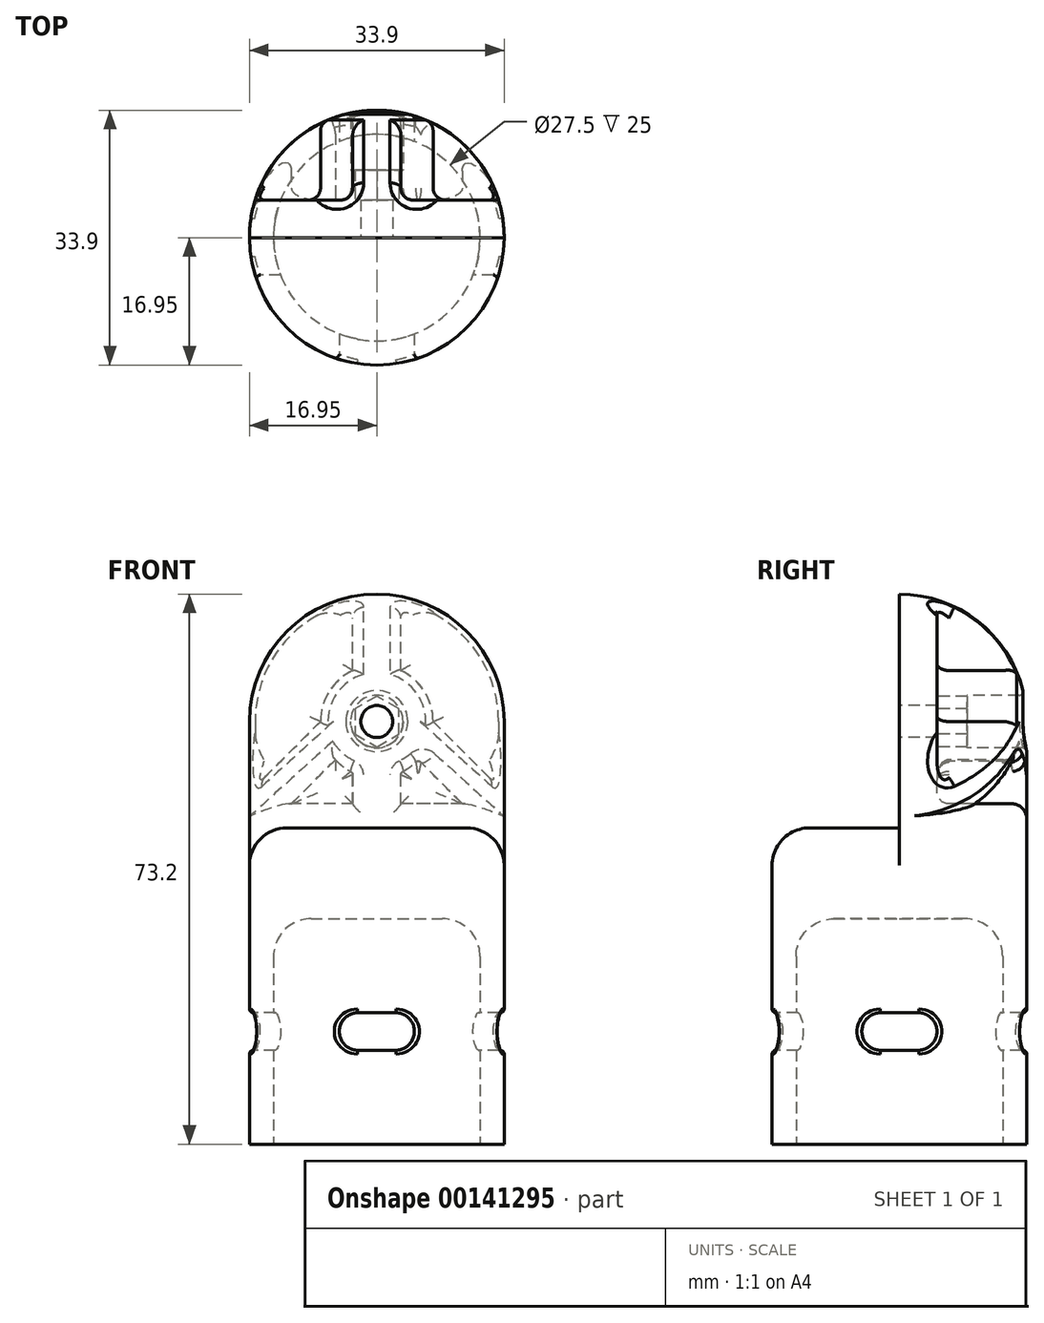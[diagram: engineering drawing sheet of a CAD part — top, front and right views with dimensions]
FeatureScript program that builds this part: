
annotation { "Feature Type Name" : "Feature", "Feature Type Description" : "" }
export const myFeature = defineFeature(function(context is Context, id is Id, definition is map)
    precondition{}
    {
        {
            var Q0;
            Q0=qCreatedBy(makeId("Front.planeOp"),FACE);
            var sketch = newSketch(context, id + "F0", { "sketchPlane" : qUnion([Q0])});
            skLineSegment(sketch, "E0", {"start": v(13.75, 0) * mm, "end": v(13.75, 25) * mm});
            skLineSegment(sketch, "E1", {"start": v(8.75, 30) * mm, "end": v(0, 30) * mm});
            skLineSegment(sketch, "E2", {"start": v(0, 30) * mm, "end": v(0, 33.2) * mm});
            skLineSegment(sketch, "E3", {"start": v(0, 33.2) * mm, "end": v(16.95, 33.2) * mm, "construction": true});
            skLineSegment(sketch, "E4", {"start": v(16.95, 33.2) * mm, "end": v(16.95, 0) * mm});
            skLineSegment(sketch, "E5", {"start": v(16.95, 0) * mm, "end": v(13.75, 0) * mm});
            skPoint(sketch, "E6.visualSharp", {"position": v(13.75, 30) * mm});
            skArc(sketch, "E6.filletArc", {"start": v(13.75, 25) * mm, "mid": v(12.29, 28.54) * mm, "end": v(8.75, 30) * mm});
            skLineSegment(sketch, "E7", {"start": v(16.95, 33.2) * mm, "end": v(16.95, 56.25) * mm});
            skLineSegment(sketch, "E8", {"start": v(0, 73.2) * mm, "end": v(0, 73.2) * mm});
            skLineSegment(sketch, "E9", {"start": v(0, 73.2) * mm, "end": v(0, 33.2) * mm});
            skPoint(sketch, "E10.visualSharp", {"position": v(16.95, 73.2) * mm});
            skArc(sketch, "E10.filletArc", {"start": v(16.95, 56.25) * mm, "mid": v(11.99, 68.24) * mm, "end": v(0, 73.2) * mm});
            skSolve(sketch);
        }
        {
            var Q0;
            Q0=qSketchRegion(id+"F0",true);
            var Q1;
            Q1=sQuery(id+"F0.wireOp",EDGE,"E2");
            revolve(context, id + "F1", {"entities" : qUnion([Q0]), "axis" : qUnion([Q1]), "revolveType" : RevolveType.FULL});
        }
        {
            var Q0;
            Q0=qCreatedBy(makeId("Front.planeOp"),FACE);
            var sketch = newSketch(context, id + "F2", { "sketchPlane" : qUnion([Q0])});
            skArc(sketch, "E11", {"start": v(20.45, 56.25) * mm, "mid": v(0, 76.7) * mm, "end": v(-20.45, 56.25) * mm});
            skLineSegment(sketch, "E12", {"start": v(-20.45, 56.25) * mm, "end": v(-20.45, 42.1) * mm});
            skLineSegment(sketch, "E13", {"start": v(-20.45, 42.1) * mm, "end": v(20.45, 42.1) * mm});
            skLineSegment(sketch, "E14", {"start": v(20.45, 42.1) * mm, "end": v(20.45, 56.25) * mm});
            skSolve(sketch);
        }
        {
            var Q0;
            Q0=qSketchRegion(id+"F2",true);
            extrude(context, id + "F3", {"entities" : qUnion([Q0]), "operationType" : NewBodyOperationType.REMOVE, "depth" : 25 * mm});
        }
        {
            var Q0;
            Q0=qCreatedBy(makeId("Front.planeOp"),FACE);
            cPlane(context, id + "F4", {"entities" : qUnion([Q0]), "cplaneType" : CPlaneType.OFFSET, "offset" : 5 * mm, "oppositeDirection" : true, "width" : 150 * mm, "height" : 150 * mm});
        }
        {
            var Q0;
            Q0=makeQuery(id+"F3.boolean.opBoolean","INTERSECT",EDGE,{"derivedFrom":[makeQuery(id+"F1.opRevolve","SWEPT_FACE",FACE,{"disambiguationData":[OSD([sQuery(id+"F0.wireOp",EDGE,"E4"),sQuery(id+"F0.wireOp",EDGE,"E7")])]}),makeQuery(id+"F3.opExtrude","SWEPT_FACE",FACE,{"disambiguationData":[OSD([sQuery(id+"F2.wireOp",EDGE,"E13")])]})]});
            fillet(context, id + "F5", {"entities" : qUnion([Q0]), "radius" : 5 * mm, "tangentPropagation" : true, "allowEdgeOverflow" : false});
        }
        {
            var Q0;
            Q0=qCreatedBy(makeId("Front.planeOp"),FACE);
            var sketch = newSketch(context, id + "F6", { "sketchPlane" : qUnion([Q0])});
            skLineSegment(sketch, "E15.bottom", {"start": v(2.5, 12.5) * mm, "end": v(-2.5, 12.5) * mm});
            skLineSegment(sketch, "E15.top", {"start": v(2.5, 17.5) * mm, "end": v(-2.5, 17.5) * mm});
            skLineSegment(sketch, "E15.left", {"start": v(5, 15) * mm, "end": v(5, 15) * mm});
            skLineSegment(sketch, "E15.right", {"start": v(-5, 15) * mm, "end": v(-5, 15) * mm});
            skPoint(sketch, "E15.middle", {"position": v(0, 15) * mm});
            skPoint(sketch, "E16.visualSharp", {"position": v(-5, 17.5) * mm});
            skArc(sketch, "E16.filletArc", {"start": v(-2.5, 17.5) * mm, "mid": v(-4.27, 16.77) * mm, "end": v(-5, 15) * mm});
            skPoint(sketch, "E17.visualSharp", {"position": v(-5, 12.5) * mm});
            skArc(sketch, "E17.filletArc", {"start": v(-5, 15) * mm, "mid": v(-4.27, 13.23) * mm, "end": v(-2.5, 12.5) * mm});
            skPoint(sketch, "E18.visualSharp", {"position": v(5, 12.5) * mm});
            skArc(sketch, "E18.filletArc", {"start": v(2.5, 12.5) * mm, "mid": v(4.27, 13.23) * mm, "end": v(5, 15) * mm});
            skPoint(sketch, "E19.visualSharp", {"position": v(5, 17.5) * mm});
            skArc(sketch, "E19.filletArc", {"start": v(5, 15) * mm, "mid": v(4.27, 16.77) * mm, "end": v(2.5, 17.5) * mm});
            skSolve(sketch);
        }
        {
            var Q0;
            Q0=qSketchRegion(id+"F6",true);
            extrude(context, id + "F7", {"entities" : qUnion([Q0]), "operationType" : NewBodyOperationType.REMOVE, "endBound" : BoundingType.SYMMETRIC, "oppositeDirection" : true, "depth" : 60 * mm});
        }
        {
            var Q0;
            Q0=qCreatedBy(makeId("Right.planeOp"),FACE);
            var sketch = newSketch(context, id + "F8", { "sketchPlane" : qUnion([Q0])});
            skLineSegment(sketch, "E20.bottom", {"start": v(2.5, 12.5) * mm, "end": v(-2.5, 12.5) * mm});
            skLineSegment(sketch, "E20.top", {"start": v(2.5, 17.5) * mm, "end": v(-2.5, 17.5) * mm});
            skLineSegment(sketch, "E20.left", {"start": v(5, 15) * mm, "end": v(5, 15) * mm});
            skLineSegment(sketch, "E20.right", {"start": v(-5, 15) * mm, "end": v(-5, 15) * mm});
            skPoint(sketch, "E20.middle", {"position": v(0, 15) * mm});
            skPoint(sketch, "E21.visualSharp", {"position": v(-5, 17.5) * mm});
            skArc(sketch, "E21.filletArc", {"start": v(-2.5, 17.5) * mm, "mid": v(-4.27, 16.77) * mm, "end": v(-5, 15) * mm});
            skPoint(sketch, "E22.visualSharp", {"position": v(5, 17.5) * mm});
            skArc(sketch, "E22.filletArc", {"start": v(5, 15) * mm, "mid": v(4.27, 16.77) * mm, "end": v(2.5, 17.5) * mm});
            skPoint(sketch, "E23.visualSharp", {"position": v(5, 12.5) * mm});
            skArc(sketch, "E23.filletArc", {"start": v(2.5, 12.5) * mm, "mid": v(4.27, 13.23) * mm, "end": v(5, 15) * mm});
            skPoint(sketch, "E24.visualSharp", {"position": v(-5, 12.5) * mm});
            skArc(sketch, "E24.filletArc", {"start": v(-5, 15) * mm, "mid": v(-4.27, 13.23) * mm, "end": v(-2.5, 12.5) * mm});
            skSolve(sketch);
        }
        {
            var Q0;
            Q0=qSketchRegion(id+"F8",true);
            extrude(context, id + "F9", {"entities" : qUnion([Q0]), "operationType" : NewBodyOperationType.REMOVE, "endBound" : BoundingType.SYMMETRIC, "depth" : 60 * mm});
        }
        {
            var Q0;
            Q0=qCreatedBy(id+"F4.planeOp",FACE);
            var sketch = newSketch(context, id + "F10", { "sketchPlane" : qUnion([Q0])});
            skArc(sketch, "E25", {"start": v(-16.95, 56.25) * mm, "mid": v(-13.07, 67.04) * mm, "end": v(-3.2, 72.9) * mm});
            skLineSegment(sketch, "E26", {"start": v(16.95, 56.25) * mm, "end": v(16.95, 46.8) * mm});
            skLineSegment(sketch, "E27", {"start": v(11.38, 45.3) * mm, "end": v(3.2, 45.3) * mm});
            skLineSegment(sketch, "E28", {"start": v(-16.95, 46.8) * mm, "end": v(-16.95, 56.25) * mm});
            skArc(sketch, "E29", {"start": v(7.5, 56.25) * mm, "mid": v(6.33, 60.27) * mm, "end": v(3.2, 63.03) * mm});
            skLineSegment(sketch, "E30.left", {"start": v(3.2, 45.3) * mm, "end": v(3.2, 49.47) * mm});
            skLineSegment(sketch, "E30.right", {"start": v(-3.2, 45.3) * mm, "end": v(-3.2, 49.47) * mm});
            skLineSegment(sketch, "E31", {"start": v(-16.95, 46.8) * mm, "end": v(-7.5, 56.25) * mm});
            skLineSegment(sketch, "E32", {"start": v(16.95, 46.8) * mm, "end": v(7.5, 56.25) * mm});
            skLineSegment(sketch, "E33", {"start": v(3.2, 63.03) * mm, "end": v(3.2, 72.9) * mm});
            skLineSegment(sketch, "E34", {"start": v(-3.2, 63.03) * mm, "end": v(-3.2, 72.9) * mm});
            skArc(sketch, "E35.trimOffspring", {"start": v(-3.2, 63.03) * mm, "mid": v(-6.33, 60.27) * mm, "end": v(-7.5, 56.25) * mm});
            skArc(sketch, "E36.trimOffspring", {"start": v(3.2, 72.9) * mm, "mid": v(13.07, 67.04) * mm, "end": v(16.95, 56.25) * mm});
            skLineSegment(sketch, "E37", {"start": v(11.38, 45.3) * mm, "end": v(5.51, 51.17) * mm});
            skLineSegment(sketch, "E38", {"start": v(-11.38, 45.3) * mm, "end": v(-5.51, 51.17) * mm});
            skArc(sketch, "E39", {"start": v(3.2, 49.47) * mm, "mid": v(4.44, 50.2) * mm, "end": v(5.51, 51.17) * mm});
            skArc(sketch, "E40", {"start": v(-3.2, 49.47) * mm, "mid": v(-4.44, 50.2) * mm, "end": v(-5.51, 51.17) * mm});
            skCircle(sketch, "E41", {"center": v(0, 56.25) * mm, "radius": 3.5 * mm});
            skLineSegment(sketch, "E42.trimOffspring", {"start": v(-3.2, 45.3) * mm, "end": v(-11.38, 45.3) * mm});
            skSolve(sketch);
        }
        {
            var Q0;
            Q0=qSketchRegion(id+"F10",true);
            extrude(context, id + "F11", {"entities" : qUnion([Q0]), "operationType" : NewBodyOperationType.REMOVE, "endBound" : BoundingType.THROUGH_ALL, "oppositeDirection" : true, "depth" : 25 * mm});
        }
        {
            var Q0;
            Q0=makeQuery(id+"F3.boolean.opBoolean","COPY",FACE,{"derivedFrom":makeQuery(id+"F3.opExtrude","CAP_FACE",FACE,{"disambiguationData":[OSD([sQuery(id+"F2.wireOp",EDGE,"E11"),sQuery(id+"F2.wireOp",EDGE,"E12"),sQuery(id+"F2.wireOp",EDGE,"E13"),sQuery(id+"F2.wireOp",EDGE,"E14")])],"isStart":true})});
            var sketch = newSketch(context, id + "F12", { "sketchPlane" : qUnion([Q0])});
            skCircle(sketch, "E43", {"center": v(0, 56.25) * mm, "radius": 2.12 * mm});
            skSolve(sketch);
        }
        {
            var Q0;
            Q0=qSketchRegion(id+"F12",true);
            extrude(context, id + "F13", {"entities" : qUnion([Q0]), "operationType" : NewBodyOperationType.REMOVE, "endBound" : BoundingType.THROUGH_ALL, "oppositeDirection" : true, "depth" : 25 * mm});
        }
        {
            var Q0;
            Q0=makeQuery(id+"F11.boolean.opBoolean","INTERSECT",EDGE,{"derivedFrom":[makeQuery(id+"F1.opRevolve","SWEPT_FACE",FACE,{"disambiguationData":[OSD([sQuery(id+"F0.wireOp",EDGE,"E10.filletArc")])]}),makeQuery(id+"F11.opExtrude","SWEPT_FACE",FACE,{"disambiguationData":[OSD([sQuery(id+"F10.wireOp",EDGE,"E41")])]})]});
            var Q1;
            Q1=makeQuery(id+"F11.boolean.opBoolean","INTERSECT",EDGE,{"derivedFrom":[makeQuery(id+"F1.opRevolve","SWEPT_FACE",FACE,{"disambiguationData":[OSD([sQuery(id+"F0.wireOp",EDGE,"E4"),sQuery(id+"F0.wireOp",EDGE,"E7")])]}),makeQuery(id+"F11.opExtrude","SWEPT_FACE",FACE,{"disambiguationData":[OSD([sQuery(id+"F10.wireOp",EDGE,"E41")])]})]});
            var Q2;
            Q2=makeQuery(id+"F7.boolean.opBoolean","INTERSECT",EDGE,{"disambiguationData":[OD(1.0)],"derivedFrom":[makeQuery(id+"F1.opRevolve","SWEPT_FACE",FACE,{"disambiguationData":[OSD([sQuery(id+"F0.wireOp",EDGE,"E4"),sQuery(id+"F0.wireOp",EDGE,"E7")])]}),makeQuery(id+"F7.opExtrude","SWEPT_FACE",FACE,{"disambiguationData":[OSD([sQuery(id+"F6.wireOp",EDGE,"E16.filletArc"),sQuery(id+"F6.wireOp",EDGE,"E17.filletArc")])]})]});
            var Q3;
            Q3=makeQuery(id+"F9.boolean.opBoolean","INTERSECT",EDGE,{"disambiguationData":[OD(1.0)],"derivedFrom":[makeQuery(id+"F1.opRevolve","SWEPT_FACE",FACE,{"disambiguationData":[OSD([sQuery(id+"F0.wireOp",EDGE,"E4"),sQuery(id+"F0.wireOp",EDGE,"E7")])]}),makeQuery(id+"F9.opExtrude","SWEPT_FACE",FACE,{"disambiguationData":[OSD([sQuery(id+"F8.wireOp",EDGE,"E22.filletArc"),sQuery(id+"F8.wireOp",EDGE,"E23.filletArc")])]})]});
            var Q4;
            Q4=makeQuery(id+"F7.boolean.opBoolean","INTERSECT",EDGE,{"disambiguationData":[OD(0.0)],"derivedFrom":[makeQuery(id+"F1.opRevolve","SWEPT_FACE",FACE,{"disambiguationData":[OSD([sQuery(id+"F0.wireOp",EDGE,"E4"),sQuery(id+"F0.wireOp",EDGE,"E7")])]}),makeQuery(id+"F7.opExtrude","SWEPT_FACE",FACE,{"disambiguationData":[OSD([sQuery(id+"F6.wireOp",EDGE,"E18.filletArc"),sQuery(id+"F6.wireOp",EDGE,"E19.filletArc")])]})]});
            var Q5;
            Q5=makeQuery(id+"F9.boolean.opBoolean","INTERSECT",EDGE,{"disambiguationData":[OD(0.0)],"derivedFrom":[makeQuery(id+"F1.opRevolve","SWEPT_FACE",FACE,{"disambiguationData":[OSD([sQuery(id+"F0.wireOp",EDGE,"E4"),sQuery(id+"F0.wireOp",EDGE,"E7")])]}),makeQuery(id+"F9.opExtrude","SWEPT_FACE",FACE,{"disambiguationData":[OSD([sQuery(id+"F8.wireOp",EDGE,"E21.filletArc"),sQuery(id+"F8.wireOp",EDGE,"E24.filletArc")])]})]});
            var Q6;
            Q6=makeQuery(id+"F11.boolean.opBoolean","COPY",EDGE,{"derivedFrom":makeQuery(id+"F11.opExtrude","SWEPT_EDGE",EDGE,{"disambiguationData":[OSD([sQuery(id+"F10.wireOp",EDGE,"E30.left"),sQuery(id+"F10.wireOp",EDGE,"E39")])]})});
            var Q7;
            Q7=makeQuery(id+"F11.boolean.opBoolean","COPY",EDGE,{"derivedFrom":makeQuery(id+"F11.opExtrude","SWEPT_EDGE",EDGE,{"disambiguationData":[OSD([sQuery(id+"F10.wireOp",EDGE,"E37"),sQuery(id+"F10.wireOp",EDGE,"E39")])]})});
            var Q8;
            Q8=makeQuery(id+"F11.boolean.opBoolean","COPY",EDGE,{"derivedFrom":makeQuery(id+"F11.opExtrude","SWEPT_EDGE",EDGE,{"disambiguationData":[OSD([sQuery(id+"F10.wireOp",EDGE,"E30.right"),sQuery(id+"F10.wireOp",EDGE,"E40")])]})});
            fillet(context, id + "F14", {"entities" : qUnion([Q0, Q1, Q2, Q3, Q4, Q5, Q6, Q7, Q8]), "radius" : .5 * mm, "tangentPropagation" : true, "allowEdgeOverflow" : false});
        }
        {
            var Q0;
            Q0=makeQuery(id+"F11.boolean.opBoolean","INTERSECT",EDGE,{"derivedFrom":[makeQuery(id+"F1.opRevolve","SWEPT_FACE",FACE,{"disambiguationData":[OSD([sQuery(id+"F0.wireOp",EDGE,"E10.filletArc")])]}),makeQuery(id+"F11.opExtrude","SWEPT_FACE",FACE,{"disambiguationData":[OSD([sQuery(id+"F10.wireOp",EDGE,"E33")])]})]});
            var Q1;
            Q1=makeQuery(id+"F11.boolean.opBoolean","INTERSECT",EDGE,{"derivedFrom":[makeQuery(id+"F1.opRevolve","SWEPT_FACE",FACE,{"disambiguationData":[OSD([sQuery(id+"F0.wireOp",EDGE,"E10.filletArc")])]}),makeQuery(id+"F11.opExtrude","SWEPT_FACE",FACE,{"disambiguationData":[OSD([sQuery(id+"F10.wireOp",EDGE,"E34")])]})]});
            var Q2;
            Q2=makeQuery(id+"F11.boolean.opBoolean","INTERSECT",EDGE,{"derivedFrom":[makeQuery(id+"F1.opRevolve","SWEPT_FACE",FACE,{"disambiguationData":[OSD([sQuery(id+"F0.wireOp",EDGE,"E10.filletArc")])]}),makeQuery(id+"F11.opExtrude","SWEPT_FACE",FACE,{"disambiguationData":[OSD([sQuery(id+"F10.wireOp",EDGE,"E35.trimOffspring")])]})]});
            var Q3;
            Q3=makeQuery(id+"F11.boolean.opBoolean","INTERSECT",EDGE,{"derivedFrom":[makeQuery(id+"F1.opRevolve","SWEPT_FACE",FACE,{"disambiguationData":[OSD([sQuery(id+"F0.wireOp",EDGE,"E10.filletArc")])]}),makeQuery(id+"F11.opExtrude","SWEPT_FACE",FACE,{"disambiguationData":[OSD([sQuery(id+"F10.wireOp",EDGE,"E29")])]})]});
            var Q4;
            Q4=makeQuery(id+"F11.boolean.opBoolean","INTERSECT",EDGE,{"derivedFrom":[makeQuery(id+"F1.opRevolve","SWEPT_FACE",FACE,{"disambiguationData":[OSD([sQuery(id+"F0.wireOp",EDGE,"E4"),sQuery(id+"F0.wireOp",EDGE,"E7")])]}),makeQuery(id+"F11.opExtrude","SWEPT_FACE",FACE,{"disambiguationData":[OSD([sQuery(id+"F10.wireOp",EDGE,"E32")])]})]});
            var Q5;
            Q5=makeQuery(id+"F11.boolean.opBoolean","INTERSECT",EDGE,{"derivedFrom":[makeQuery(id+"F1.opRevolve","SWEPT_FACE",FACE,{"disambiguationData":[OSD([sQuery(id+"F0.wireOp",EDGE,"E4"),sQuery(id+"F0.wireOp",EDGE,"E7")])]}),makeQuery(id+"F11.opExtrude","SWEPT_FACE",FACE,{"disambiguationData":[OSD([sQuery(id+"F10.wireOp",EDGE,"E31")])]})]});
            var Q6;
            Q6=makeQuery(id+"F11.boolean.opBoolean","INTERSECT",EDGE,{"derivedFrom":[makeQuery(id+"F1.opRevolve","SWEPT_FACE",FACE,{"disambiguationData":[OSD([sQuery(id+"F0.wireOp",EDGE,"E4"),sQuery(id+"F0.wireOp",EDGE,"E7")])]}),makeQuery(id+"F11.opExtrude","SWEPT_FACE",FACE,{"disambiguationData":[OSD([sQuery(id+"F10.wireOp",EDGE,"E38")])]})]});
            var Q7;
            Q7=makeQuery(id+"F11.boolean.opBoolean","INTERSECT",EDGE,{"derivedFrom":[makeQuery(id+"F1.opRevolve","SWEPT_FACE",FACE,{"disambiguationData":[OSD([sQuery(id+"F0.wireOp",EDGE,"E4"),sQuery(id+"F0.wireOp",EDGE,"E7")])]}),makeQuery(id+"F11.opExtrude","SWEPT_FACE",FACE,{"disambiguationData":[OSD([sQuery(id+"F10.wireOp",EDGE,"E42.trimOffspring")])]})]});
            var Q8;
            Q8=makeQuery(id+"F11.boolean.opBoolean","INTERSECT",EDGE,{"derivedFrom":[makeQuery(id+"F1.opRevolve","SWEPT_FACE",FACE,{"disambiguationData":[OSD([sQuery(id+"F0.wireOp",EDGE,"E4"),sQuery(id+"F0.wireOp",EDGE,"E7")])]}),makeQuery(id+"F11.opExtrude","SWEPT_FACE",FACE,{"disambiguationData":[OSD([sQuery(id+"F10.wireOp",EDGE,"E30.right")])]})]});
            var Q9;
            Q9=makeQuery(id+"F11.boolean.opBoolean","INTERSECT",EDGE,{"derivedFrom":[makeQuery(id+"F1.opRevolve","SWEPT_FACE",FACE,{"disambiguationData":[OSD([sQuery(id+"F0.wireOp",EDGE,"E4"),sQuery(id+"F0.wireOp",EDGE,"E7")])]}),makeQuery(id+"F11.opExtrude","SWEPT_FACE",FACE,{"disambiguationData":[OSD([sQuery(id+"F10.wireOp",EDGE,"E30.left")])]})]});
            var Q10;
            Q10=makeQuery(id+"F11.boolean.opBoolean","INTERSECT",EDGE,{"derivedFrom":[makeQuery(id+"F1.opRevolve","SWEPT_FACE",FACE,{"disambiguationData":[OSD([sQuery(id+"F0.wireOp",EDGE,"E4"),sQuery(id+"F0.wireOp",EDGE,"E7")])]}),makeQuery(id+"F11.opExtrude","SWEPT_FACE",FACE,{"disambiguationData":[OSD([sQuery(id+"F10.wireOp",EDGE,"E27")])]})]});
            var Q11;
            Q11=makeQuery(id+"F11.boolean.opBoolean","COPY",EDGE,{"derivedFrom":makeQuery(id+"F11.opExtrude","CAP_EDGE",EDGE,{"disambiguationData":[OSD([sQuery(id+"F10.wireOp",EDGE,"E34")])],"isStart":true})});
            var Q12;
            Q12=makeQuery(id+"F11.boolean.opBoolean","COPY",EDGE,{"derivedFrom":makeQuery(id+"F11.opExtrude","CAP_EDGE",EDGE,{"disambiguationData":[OSD([sQuery(id+"F10.wireOp",EDGE,"E35.trimOffspring")])],"isStart":true})});
            var Q13;
            Q13=makeQuery(id+"F11.boolean.opBoolean","COPY",EDGE,{"derivedFrom":makeQuery(id+"F11.opExtrude","CAP_EDGE",EDGE,{"disambiguationData":[OSD([sQuery(id+"F10.wireOp",EDGE,"E31")])],"isStart":true})});
            var Q14;
            Q14=makeQuery(id+"F11.boolean.opBoolean","COPY",EDGE,{"derivedFrom":makeQuery(id+"F11.opExtrude","CAP_EDGE",EDGE,{"disambiguationData":[OSD([sQuery(id+"F10.wireOp",EDGE,"E38")])],"isStart":true})});
            var Q15;
            Q15=makeQuery(id+"F11.boolean.opBoolean","COPY",EDGE,{"derivedFrom":makeQuery(id+"F11.opExtrude","CAP_EDGE",EDGE,{"disambiguationData":[OSD([sQuery(id+"F10.wireOp",EDGE,"E42.trimOffspring")])],"isStart":true})});
            var Q16;
            Q16=makeQuery(id+"F11.boolean.opBoolean","COPY",EDGE,{"derivedFrom":makeQuery(id+"F11.opExtrude","CAP_EDGE",EDGE,{"disambiguationData":[OSD([sQuery(id+"F10.wireOp",EDGE,"E30.right")])],"isStart":true})});
            var Q17;
            Q17=makeQuery(id+"F11.boolean.opBoolean","COPY",EDGE,{"derivedFrom":makeQuery(id+"F11.opExtrude","CAP_EDGE",EDGE,{"disambiguationData":[OSD([sQuery(id+"F10.wireOp",EDGE,"E30.left")])],"isStart":true})});
            var Q18;
            Q18=makeQuery(id+"F11.boolean.opBoolean","COPY",EDGE,{"derivedFrom":makeQuery(id+"F11.opExtrude","CAP_EDGE",EDGE,{"disambiguationData":[OSD([sQuery(id+"F10.wireOp",EDGE,"E27")])],"isStart":true})});
            var Q19;
            Q19=makeQuery(id+"F11.boolean.opBoolean","COPY",EDGE,{"derivedFrom":makeQuery(id+"F11.opExtrude","CAP_EDGE",EDGE,{"disambiguationData":[OSD([sQuery(id+"F10.wireOp",EDGE,"E33")])],"isStart":true})});
            var Q20;
            Q20=makeQuery(id+"F11.boolean.opBoolean","COPY",EDGE,{"derivedFrom":makeQuery(id+"F11.opExtrude","CAP_EDGE",EDGE,{"disambiguationData":[OSD([sQuery(id+"F10.wireOp",EDGE,"E29")])],"isStart":true})});
            var Q21;
            Q21=makeQuery(id+"F11.boolean.opBoolean","COPY",EDGE,{"derivedFrom":makeQuery(id+"F11.opExtrude","CAP_EDGE",EDGE,{"disambiguationData":[OSD([sQuery(id+"F10.wireOp",EDGE,"E32")])],"isStart":true})});
            fillet(context, id + "F15", {"entities" : qUnion([Q0, Q1, Q2, Q3, Q4, Q5, Q6, Q7, Q8, Q9, Q10, Q11, Q12, Q13, Q14, Q15, Q16, Q17, Q18, Q19, Q20, Q21]), "radius" : 1.6 * mm, "tangentPropagation" : true, "allowEdgeOverflow" : false});
        }
        {
            var Q0;
            Q0=makeQuery(id+"F11.boolean.opBoolean","COPY",FACE,{"derivedFrom":makeQuery(id+"F11.opExtrude","CAP_FACE",FACE,{"disambiguationData":[OSD([sQuery(id+"F10.wireOp",EDGE,"E41")])],"isStart":true})});
            var sketch = newSketch(context, id + "F16", { "sketchPlane" : qUnion([Q0])});
            skCircle(sketch, "E44.cCircle", {"center": v(0, 56.25) * mm, "radius": 2.93 * mm, "construction": true});
            skLineSegment(sketch, "E44.0", {"start": v(2.93, 57.94) * mm, "end": v(2.93, 54.56) * mm});
            skLineSegment(sketch, "E44.1", {"start": v(2.93, 54.56) * mm, "end": v(0, 52.87) * mm});
            skLineSegment(sketch, "E44.2", {"start": v(0, 52.87) * mm, "end": v(-2.92, 54.56) * mm});
            skLineSegment(sketch, "E44.3", {"start": v(-2.92, 54.56) * mm, "end": v(-2.93, 57.94) * mm});
            skLineSegment(sketch, "E44.4", {"start": v(-2.93, 57.94) * mm, "end": v(0, 59.63) * mm});
            skLineSegment(sketch, "E44.5", {"start": v(0, 59.63) * mm, "end": v(2.93, 57.94) * mm});
            skPoint(sketch, "E44.0.midPoint", {"position": v(2.93, 56.25) * mm});
            skCircle(sketch, "E45", {"center": v(0, 56.25) * mm, "radius": 3.5 * mm});
            skSolve(sketch);
        }
        {
            var Q0;
            Q0 = qSketchRegion(id + "F16", true);
            extrude(context, id + "F17", {"entities" : qUnion([Q0]), "operationType" : NewBodyOperationType.ADD, "depth" : 4 * mm});
        }
    });
